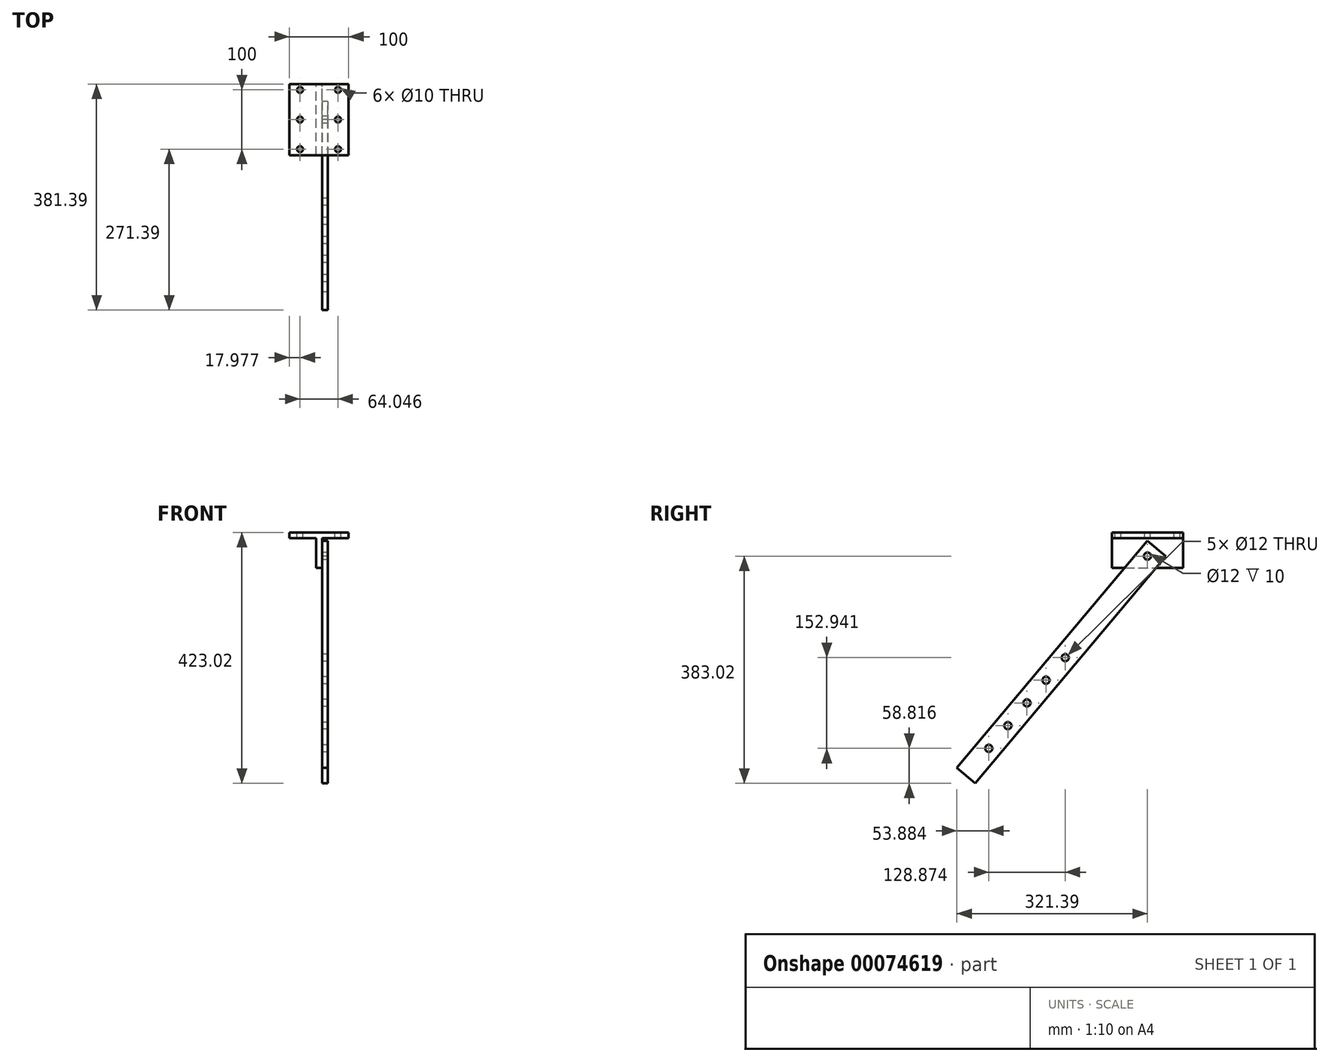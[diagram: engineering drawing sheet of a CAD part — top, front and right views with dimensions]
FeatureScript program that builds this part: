
annotation { "Feature Type Name" : "Feature", "Feature Type Description" : "" }
export const myFeature = defineFeature(function(context is Context, id is Id, definition is map)
    precondition{}
    {
        {
            var Q0;
            Q0=qCreatedBy(makeId("Front.planeOp"),FACE);
            var sketch = newSketch(context, id + "F0", { "sketchPlane" : qUnion([Q0])});
            skLineSegment(sketch, "E0", {"start": v(-5, 0) * mm, "end": v(-5, 50) * mm});
            skLineSegment(sketch, "E1", {"start": v(-5, 50) * mm, "end": v(-50, 50) * mm});
            skLineSegment(sketch, "E2", {"start": v(-50, 50) * mm, "end": v(-50, 60) * mm});
            skLineSegment(sketch, "E3", {"start": v(0, 0) * mm, "end": v(0, 96.9) * mm, "construction": true});
            skLineSegment(sketch, "E4.MirrorCS", {"start": v(5, 0) * mm, "end": v(5, 50) * mm});
            skLineSegment(sketch, "E5.MirrorCS", {"start": v(50, 50) * mm, "end": v(50, 60) * mm});
            skLineSegment(sketch, "E6.MirrorCS", {"start": v(5, 50) * mm, "end": v(50, 50) * mm});
            skLineSegment(sketch, "E7", {"start": v(-50, 60) * mm, "end": v(50, 60) * mm});
            skLineSegment(sketch, "E8", {"start": v(-5, 0) * mm, "end": v(5, 0) * mm});
            skSolve(sketch);
        }
        {
            var Q0;
            Q0 = qSketchRegion(id + "F0", true);
            extrude(context, id + "F1", {"entities" : qUnion([Q0]), "depth" : 120 * mm});
        }
        {
            var Q0;
            Q0=makeQuery(id+"F1.opExtrude","SWEPT_FACE",FACE,{"disambiguationData":[OSD([sQuery(id+"F0.wireOp",EDGE,"E4.MirrorCS")])]});
            var sketch = newSketch(context, id + "F2", { "sketchPlane" : qUnion([Q0])});
            skLineSegment(sketch, "E9", {"start": v(-60, 45.71) * mm, "end": v(-381.4, -337.31) * mm});
            skLineSegment(sketch, "E10", {"start": v(-381.4, -337.31) * mm, "end": v(-350.75, -363.02) * mm});
            skLineSegment(sketch, "E11", {"start": v(-350.75, -363.02) * mm, "end": v(-29.36, 20) * mm});
            skLineSegment(sketch, "E12", {"start": v(-29.36, 20) * mm, "end": v(-60, 45.71) * mm});
            skLineSegment(sketch, "E13", {"start": v(-60, 45.71) * mm, "end": v(-60, -16.52) * mm, "construction": true});
            skLineSegment(sketch, "E14", {"start": v(-29.36, 20) * mm, "end": v(-81.57, 20) * mm, "construction": true});
            skCircle(sketch, "E15", {"center": v(-60, 20) * mm, "radius": 6 * mm});
            skLineSegment(sketch, "E16", {"start": v(-44.68, 32.86) * mm, "end": v(-366.07, -350.17) * mm, "construction": true});
            skCircle(sketch, "E17", {"center": v(-327.5, -304.2) * mm, "radius": 6 * mm});
            skCircle(sketch, "E18", {"center": v(-295.37, -265.9) * mm, "radius": 6 * mm});
            skCircle(sketch, "E19", {"center": v(-263.23, -227.6) * mm, "radius": 6 * mm});
            skCircle(sketch, "E20", {"center": v(-231.09, -189.3) * mm, "radius": 6 * mm});
            skCircle(sketch, "E21", {"center": v(-198.63, -151.26) * mm, "radius": 6 * mm});
            skSolve(sketch);
        }
        {
            var Q0;
            Q0 = qSketchRegion(id + "F2", true);
            extrude(context, id + "F3", {"entities" : qUnion([Q0]), "operationType" : NewBodyOperationType.ADD, "depth" : 10 * mm});
        }
        {
            var Q0;
            Q0=makeQuery(id+"F1.opExtrude","SWEPT_FACE",FACE,{"disambiguationData":[OSD([sQuery(id+"F0.wireOp",EDGE,"E7")])]});
            var sketch = newSketch(context, id + "F4", { "sketchPlane" : qUnion([Q0])});
            skCircle(sketch, "E22", {"center": v(-32.02, -10) * mm, "radius": 5 * mm});
            skCircle(sketch, "E23", {"center": v(-32.02, -60) * mm, "radius": 5 * mm});
            skCircle(sketch, "E24", {"center": v(-32.02, -110) * mm, "radius": 5 * mm});
            skLineSegment(sketch, "E25", {"start": v(-50, -60) * mm, "end": v(50, -60) * mm, "construction": true});
            skLineSegment(sketch, "E26", {"start": v(-32.02, 0) * mm, "end": v(-32.02, -120) * mm, "construction": true});
            skLineSegment(sketch, "E27", {"start": v(0, 0) * mm, "end": v(0, -120) * mm, "construction": true});
            skCircle(sketch, "E28.MirrorC", {"center": v(32.02, -110) * mm, "radius": 5 * mm});
            skCircle(sketch, "E29.MirrorC", {"center": v(32.02, -60) * mm, "radius": 5 * mm});
            skCircle(sketch, "E30.MirrorC", {"center": v(32.02, -10) * mm, "radius": 5 * mm});
            skSolve(sketch);
        }
        {
            var Q0;
            Q0 = qSketchRegion(id + "F4", true);
            extrude(context, id + "F5", {"entities" : qUnion([Q0]), "operationType" : NewBodyOperationType.REMOVE, "endBound" : BoundingType.THROUGH_ALL, "oppositeDirection" : true, "depth" : 25 * mm});
        }
    });
